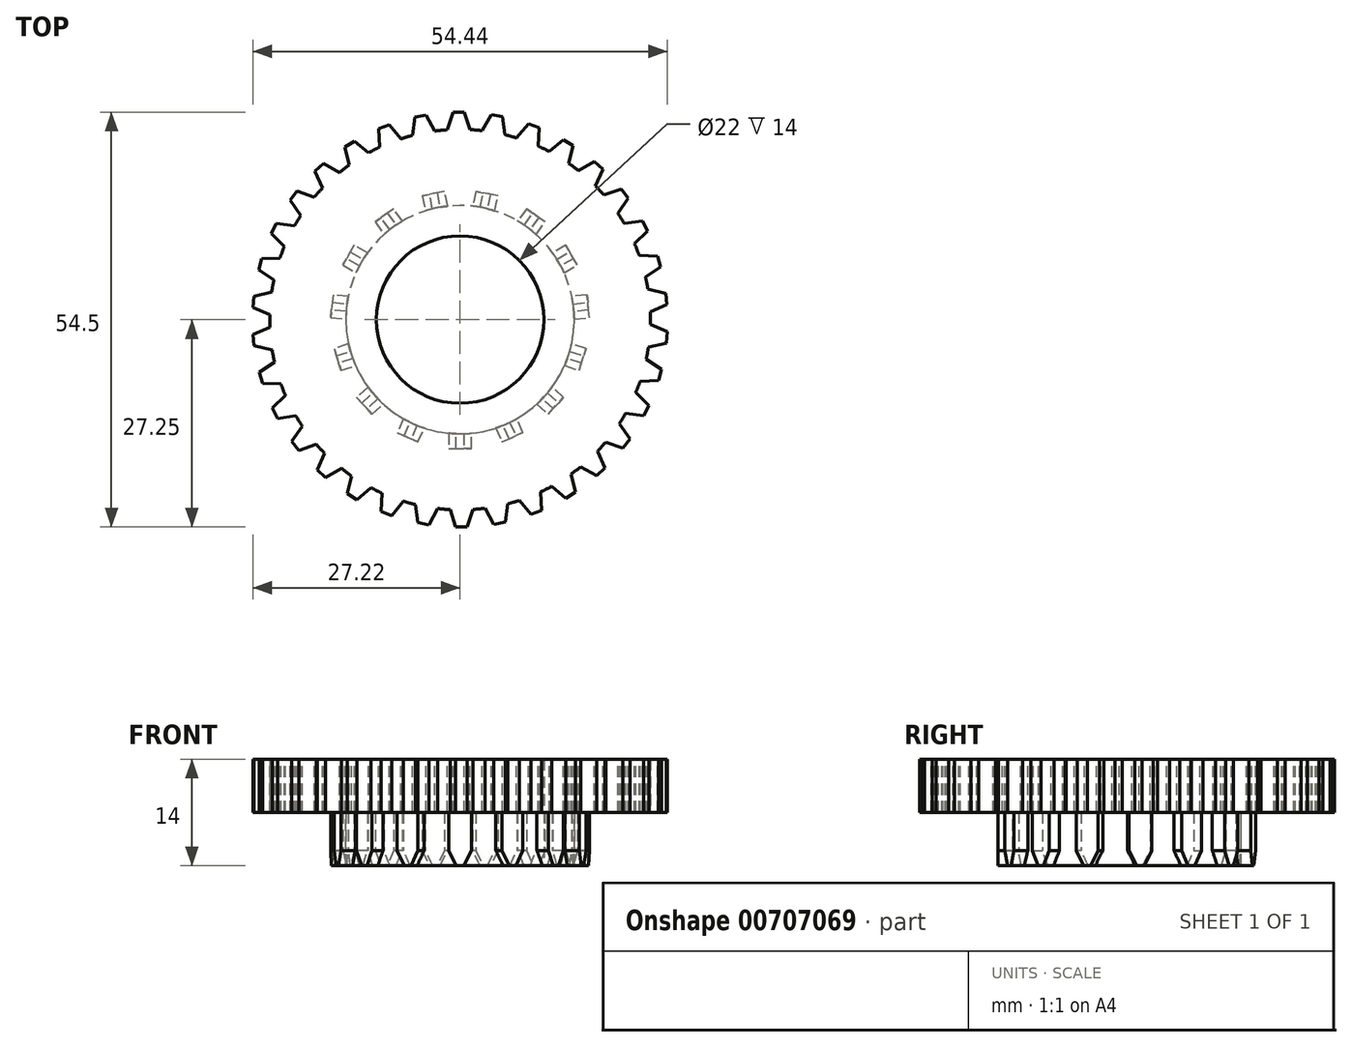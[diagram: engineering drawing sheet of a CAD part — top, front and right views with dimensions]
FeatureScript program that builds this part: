
annotation { "Feature Type Name" : "Feature", "Feature Type Description" : "" }
export const myFeature = defineFeature(function(context is Context, id is Id, definition is map)
    precondition{}
    {
        {
            var Q0;
            Q0=qCreatedBy(makeId("Top.planeOp"),FACE);
            var sketch = newSketch(context, id + "F0", { "sketchPlane" : qUnion([Q0])});
            skCircle(sketch, "E0", {"center": v(0, 0) * mm, "radius": 11 * mm});
            skCircle(sketch, "E1", {"center": v(0, 0) * mm, "radius": 25 * mm});
            skSolve(sketch);
        }
        {
            var Q0;
            Q0=makeQuery(id+"F0.imprint","IMPRINT",FACE,{"disambiguationData":[TD([[makeQuery(id+"F0.imprint","IMPRINT",EDGE,{"derivedFrom":sQuery(id+"F0.wireOp",EDGE,"E0")}),-1.0]])]});
            extrude(context, id + "F1", {"entities" : qUnion([Q0]), "depth" : 7 * mm, "offsetDistance" : 25 * mm});
        }
        {
            var Q0;
            Q0=makeQuery(id+"F1.opExtrude","CAP_FACE",FACE,{"disambiguationData":[OSD([sQuery(id+"F0.wireOp",EDGE,"E0"),sQuery(id+"F0.wireOp",EDGE,"E1")])],"isStart":false});
            var sketch = newSketch(context, id + "F2", { "sketchPlane" : qUnion([Q0])});
            skLineSegment(sketch, "E2", {"start": v(-1.69, 24.94) * mm, "end": v(1.31, 24.97) * mm});
            skLineSegment(sketch, "E3", {"start": v(1.31, 24.97) * mm, "end": v(0.56, 27.25) * mm});
            skLineSegment(sketch, "E4", {"start": v(0.56, 27.25) * mm, "end": v(-0.94, 27.25) * mm});
            skLineSegment(sketch, "E5", {"start": v(-0.94, 27.25) * mm, "end": v(-1.69, 24.94) * mm});
            skSolve(sketch);
        }
        {
            var Q0;
            {var subQ0=sQuery(id+"F2.wireOp",EDGE,"E3");Q0=makeQuery(id+"F2.imprint","IMPRINT",FACE,{"disambiguationData":[TD([[makeQuery(id+"F2.imprint","IMPRINT",EDGE,{"derivedFrom":subQ0}),1.0]])]});}
            extrude(context, id + "F3", {"entities" : qUnion([Q0]), "oppositeDirection" : true, "depth" : 7 * mm, "offsetDistance" : 25 * mm});
        }
        {
            var Q0;
            Q0=makeQuery(id+"F3.opExtrude","SWEPT_BODY",BODY,{"disambiguationData":[OSD([sQuery(id+"F0.wireOp",EDGE,"E1"),sQuery(id+"F2.wireOp",EDGE,"E3"),sQuery(id+"F2.wireOp",EDGE,"E4"),sQuery(id+"F2.wireOp",EDGE,"E5")])]});
            var Q1;
            Q1=makeQuery(id+"F1.opExtrude","CAP_EDGE",EDGE,{"disambiguationData":[OSD([sQuery(id+"F0.wireOp",EDGE,"E0")])],"isStart":false});
            circularPattern(context, id + "F4", {"entities" : qUnion([Q0]), "axis" : qUnion([Q1]), "angle" : 360 * degree, "instanceCount" : 34, "equalSpace" : true});
        }
        {
            var Q0;
            Q0=makeQuery(id+"F4.opPattern","COPY",BODY,{"derivedFrom":makeQuery(id+"F3.opExtrude","SWEPT_BODY",BODY,{"disambiguationData":[OSD([sQuery(id+"F0.wireOp",EDGE,"E1"),sQuery(id+"F2.wireOp",EDGE,"E3"),sQuery(id+"F2.wireOp",EDGE,"E4"),sQuery(id+"F2.wireOp",EDGE,"E5")])]}),"instanceName":"8"});
            var Q1;
            Q1=makeQuery(id+"F1.opExtrude","SWEPT_BODY",BODY,{"disambiguationData":[OSD([sQuery(id+"F0.wireOp",EDGE,"E0"),sQuery(id+"F0.wireOp",EDGE,"E1")])]});
            var Q2;
            Q2=makeQuery(id+"F4.opPattern","COPY",BODY,{"derivedFrom":makeQuery(id+"F3.opExtrude","SWEPT_BODY",BODY,{"disambiguationData":[OSD([sQuery(id+"F0.wireOp",EDGE,"E1"),sQuery(id+"F2.wireOp",EDGE,"E3"),sQuery(id+"F2.wireOp",EDGE,"E4"),sQuery(id+"F2.wireOp",EDGE,"E5")])]}),"instanceName":"9"});
            var Q3;
            Q3=makeQuery(id+"F4.opPattern","COPY",BODY,{"derivedFrom":makeQuery(id+"F3.opExtrude","SWEPT_BODY",BODY,{"disambiguationData":[OSD([sQuery(id+"F0.wireOp",EDGE,"E1"),sQuery(id+"F2.wireOp",EDGE,"E3"),sQuery(id+"F2.wireOp",EDGE,"E4"),sQuery(id+"F2.wireOp",EDGE,"E5")])]}),"instanceName":"10"});
            var Q4;
            Q4=makeQuery(id+"F4.opPattern","COPY",BODY,{"derivedFrom":makeQuery(id+"F3.opExtrude","SWEPT_BODY",BODY,{"disambiguationData":[OSD([sQuery(id+"F0.wireOp",EDGE,"E1"),sQuery(id+"F2.wireOp",EDGE,"E3"),sQuery(id+"F2.wireOp",EDGE,"E4"),sQuery(id+"F2.wireOp",EDGE,"E5")])]}),"instanceName":"11"});
            var Q5;
            Q5=makeQuery(id+"F4.opPattern","COPY",BODY,{"derivedFrom":makeQuery(id+"F3.opExtrude","SWEPT_BODY",BODY,{"disambiguationData":[OSD([sQuery(id+"F0.wireOp",EDGE,"E1"),sQuery(id+"F2.wireOp",EDGE,"E3"),sQuery(id+"F2.wireOp",EDGE,"E4"),sQuery(id+"F2.wireOp",EDGE,"E5")])]}),"instanceName":"12"});
            var Q6;
            Q6=makeQuery(id+"F4.opPattern","COPY",BODY,{"derivedFrom":makeQuery(id+"F3.opExtrude","SWEPT_BODY",BODY,{"disambiguationData":[OSD([sQuery(id+"F0.wireOp",EDGE,"E1"),sQuery(id+"F2.wireOp",EDGE,"E3"),sQuery(id+"F2.wireOp",EDGE,"E4"),sQuery(id+"F2.wireOp",EDGE,"E5")])]}),"instanceName":"13"});
            var Q7;
            Q7=makeQuery(id+"F4.opPattern","COPY",BODY,{"derivedFrom":makeQuery(id+"F3.opExtrude","SWEPT_BODY",BODY,{"disambiguationData":[OSD([sQuery(id+"F0.wireOp",EDGE,"E1"),sQuery(id+"F2.wireOp",EDGE,"E3"),sQuery(id+"F2.wireOp",EDGE,"E4"),sQuery(id+"F2.wireOp",EDGE,"E5")])]}),"instanceName":"33"});
            var Q8;
            Q8=makeQuery(id+"F3.opExtrude","SWEPT_BODY",BODY,{"disambiguationData":[OSD([sQuery(id+"F0.wireOp",EDGE,"E1"),sQuery(id+"F2.wireOp",EDGE,"E3"),sQuery(id+"F2.wireOp",EDGE,"E4"),sQuery(id+"F2.wireOp",EDGE,"E5")])]});
            var Q9;
            Q9=makeQuery(id+"F4.opPattern","COPY",BODY,{"derivedFrom":makeQuery(id+"F3.opExtrude","SWEPT_BODY",BODY,{"disambiguationData":[OSD([sQuery(id+"F0.wireOp",EDGE,"E1"),sQuery(id+"F2.wireOp",EDGE,"E3"),sQuery(id+"F2.wireOp",EDGE,"E4"),sQuery(id+"F2.wireOp",EDGE,"E5")])]}),"instanceName":"31"});
            var Q10;
            Q10=makeQuery(id+"F4.opPattern","COPY",BODY,{"derivedFrom":makeQuery(id+"F3.opExtrude","SWEPT_BODY",BODY,{"disambiguationData":[OSD([sQuery(id+"F0.wireOp",EDGE,"E1"),sQuery(id+"F2.wireOp",EDGE,"E3"),sQuery(id+"F2.wireOp",EDGE,"E4"),sQuery(id+"F2.wireOp",EDGE,"E5")])]}),"instanceName":"30"});
            var Q11;
            Q11=makeQuery(id+"F4.opPattern","COPY",BODY,{"derivedFrom":makeQuery(id+"F3.opExtrude","SWEPT_BODY",BODY,{"disambiguationData":[OSD([sQuery(id+"F0.wireOp",EDGE,"E1"),sQuery(id+"F2.wireOp",EDGE,"E3"),sQuery(id+"F2.wireOp",EDGE,"E4"),sQuery(id+"F2.wireOp",EDGE,"E5")])]}),"instanceName":"29"});
            var Q12;
            Q12=makeQuery(id+"F4.opPattern","COPY",BODY,{"derivedFrom":makeQuery(id+"F3.opExtrude","SWEPT_BODY",BODY,{"disambiguationData":[OSD([sQuery(id+"F0.wireOp",EDGE,"E1"),sQuery(id+"F2.wireOp",EDGE,"E3"),sQuery(id+"F2.wireOp",EDGE,"E4"),sQuery(id+"F2.wireOp",EDGE,"E5")])]}),"instanceName":"28"});
            var Q13;
            Q13=makeQuery(id+"F4.opPattern","COPY",BODY,{"derivedFrom":makeQuery(id+"F3.opExtrude","SWEPT_BODY",BODY,{"disambiguationData":[OSD([sQuery(id+"F0.wireOp",EDGE,"E1"),sQuery(id+"F2.wireOp",EDGE,"E3"),sQuery(id+"F2.wireOp",EDGE,"E4"),sQuery(id+"F2.wireOp",EDGE,"E5")])]}),"instanceName":"27"});
            var Q14;
            Q14=makeQuery(id+"F4.opPattern","COPY",BODY,{"derivedFrom":makeQuery(id+"F3.opExtrude","SWEPT_BODY",BODY,{"disambiguationData":[OSD([sQuery(id+"F0.wireOp",EDGE,"E1"),sQuery(id+"F2.wireOp",EDGE,"E3"),sQuery(id+"F2.wireOp",EDGE,"E4"),sQuery(id+"F2.wireOp",EDGE,"E5")])]}),"instanceName":"26"});
            var Q15;
            Q15=makeQuery(id+"F4.opPattern","COPY",BODY,{"derivedFrom":makeQuery(id+"F3.opExtrude","SWEPT_BODY",BODY,{"disambiguationData":[OSD([sQuery(id+"F0.wireOp",EDGE,"E1"),sQuery(id+"F2.wireOp",EDGE,"E3"),sQuery(id+"F2.wireOp",EDGE,"E4"),sQuery(id+"F2.wireOp",EDGE,"E5")])]}),"instanceName":"25"});
            var Q16;
            Q16=makeQuery(id+"F4.opPattern","COPY",BODY,{"derivedFrom":makeQuery(id+"F3.opExtrude","SWEPT_BODY",BODY,{"disambiguationData":[OSD([sQuery(id+"F0.wireOp",EDGE,"E1"),sQuery(id+"F2.wireOp",EDGE,"E3"),sQuery(id+"F2.wireOp",EDGE,"E4"),sQuery(id+"F2.wireOp",EDGE,"E5")])]}),"instanceName":"24"});
            var Q17;
            Q17=makeQuery(id+"F4.opPattern","COPY",BODY,{"derivedFrom":makeQuery(id+"F3.opExtrude","SWEPT_BODY",BODY,{"disambiguationData":[OSD([sQuery(id+"F0.wireOp",EDGE,"E1"),sQuery(id+"F2.wireOp",EDGE,"E3"),sQuery(id+"F2.wireOp",EDGE,"E4"),sQuery(id+"F2.wireOp",EDGE,"E5")])]}),"instanceName":"23"});
            var Q18;
            Q18=makeQuery(id+"F4.opPattern","COPY",BODY,{"derivedFrom":makeQuery(id+"F3.opExtrude","SWEPT_BODY",BODY,{"disambiguationData":[OSD([sQuery(id+"F0.wireOp",EDGE,"E1"),sQuery(id+"F2.wireOp",EDGE,"E3"),sQuery(id+"F2.wireOp",EDGE,"E4"),sQuery(id+"F2.wireOp",EDGE,"E5")])]}),"instanceName":"22"});
            var Q19;
            Q19=makeQuery(id+"F4.opPattern","COPY",BODY,{"derivedFrom":makeQuery(id+"F3.opExtrude","SWEPT_BODY",BODY,{"disambiguationData":[OSD([sQuery(id+"F0.wireOp",EDGE,"E1"),sQuery(id+"F2.wireOp",EDGE,"E3"),sQuery(id+"F2.wireOp",EDGE,"E4"),sQuery(id+"F2.wireOp",EDGE,"E5")])]}),"instanceName":"21"});
            var Q20;
            Q20=makeQuery(id+"F4.opPattern","COPY",BODY,{"derivedFrom":makeQuery(id+"F3.opExtrude","SWEPT_BODY",BODY,{"disambiguationData":[OSD([sQuery(id+"F0.wireOp",EDGE,"E1"),sQuery(id+"F2.wireOp",EDGE,"E3"),sQuery(id+"F2.wireOp",EDGE,"E4"),sQuery(id+"F2.wireOp",EDGE,"E5")])]}),"instanceName":"20"});
            var Q21;
            Q21=makeQuery(id+"F4.opPattern","COPY",BODY,{"derivedFrom":makeQuery(id+"F3.opExtrude","SWEPT_BODY",BODY,{"disambiguationData":[OSD([sQuery(id+"F0.wireOp",EDGE,"E1"),sQuery(id+"F2.wireOp",EDGE,"E3"),sQuery(id+"F2.wireOp",EDGE,"E4"),sQuery(id+"F2.wireOp",EDGE,"E5")])]}),"instanceName":"19"});
            var Q22;
            Q22=makeQuery(id+"F4.opPattern","COPY",BODY,{"derivedFrom":makeQuery(id+"F3.opExtrude","SWEPT_BODY",BODY,{"disambiguationData":[OSD([sQuery(id+"F0.wireOp",EDGE,"E1"),sQuery(id+"F2.wireOp",EDGE,"E3"),sQuery(id+"F2.wireOp",EDGE,"E4"),sQuery(id+"F2.wireOp",EDGE,"E5")])]}),"instanceName":"18"});
            var Q23;
            Q23=makeQuery(id+"F4.opPattern","COPY",BODY,{"derivedFrom":makeQuery(id+"F3.opExtrude","SWEPT_BODY",BODY,{"disambiguationData":[OSD([sQuery(id+"F0.wireOp",EDGE,"E1"),sQuery(id+"F2.wireOp",EDGE,"E3"),sQuery(id+"F2.wireOp",EDGE,"E4"),sQuery(id+"F2.wireOp",EDGE,"E5")])]}),"instanceName":"17"});
            var Q24;
            Q24=makeQuery(id+"F4.opPattern","COPY",BODY,{"derivedFrom":makeQuery(id+"F3.opExtrude","SWEPT_BODY",BODY,{"disambiguationData":[OSD([sQuery(id+"F0.wireOp",EDGE,"E1"),sQuery(id+"F2.wireOp",EDGE,"E3"),sQuery(id+"F2.wireOp",EDGE,"E4"),sQuery(id+"F2.wireOp",EDGE,"E5")])]}),"instanceName":"16"});
            var Q25;
            Q25=makeQuery(id+"F4.opPattern","COPY",BODY,{"derivedFrom":makeQuery(id+"F3.opExtrude","SWEPT_BODY",BODY,{"disambiguationData":[OSD([sQuery(id+"F0.wireOp",EDGE,"E1"),sQuery(id+"F2.wireOp",EDGE,"E3"),sQuery(id+"F2.wireOp",EDGE,"E4"),sQuery(id+"F2.wireOp",EDGE,"E5")])]}),"instanceName":"15"});
            var Q26;
            Q26=makeQuery(id+"F4.opPattern","COPY",BODY,{"derivedFrom":makeQuery(id+"F3.opExtrude","SWEPT_BODY",BODY,{"disambiguationData":[OSD([sQuery(id+"F0.wireOp",EDGE,"E1"),sQuery(id+"F2.wireOp",EDGE,"E3"),sQuery(id+"F2.wireOp",EDGE,"E4"),sQuery(id+"F2.wireOp",EDGE,"E5")])]}),"instanceName":"14"});
            var Q27;
            Q27=makeQuery(id+"F4.opPattern","COPY",BODY,{"derivedFrom":makeQuery(id+"F3.opExtrude","SWEPT_BODY",BODY,{"disambiguationData":[OSD([sQuery(id+"F0.wireOp",EDGE,"E1"),sQuery(id+"F2.wireOp",EDGE,"E3"),sQuery(id+"F2.wireOp",EDGE,"E4"),sQuery(id+"F2.wireOp",EDGE,"E5")])]}),"instanceName":"7"});
            var Q28;
            Q28=makeQuery(id+"F4.opPattern","COPY",BODY,{"derivedFrom":makeQuery(id+"F3.opExtrude","SWEPT_BODY",BODY,{"disambiguationData":[OSD([sQuery(id+"F0.wireOp",EDGE,"E1"),sQuery(id+"F2.wireOp",EDGE,"E3"),sQuery(id+"F2.wireOp",EDGE,"E4"),sQuery(id+"F2.wireOp",EDGE,"E5")])]}),"instanceName":"6"});
            var Q29;
            Q29=makeQuery(id+"F4.opPattern","COPY",BODY,{"derivedFrom":makeQuery(id+"F3.opExtrude","SWEPT_BODY",BODY,{"disambiguationData":[OSD([sQuery(id+"F0.wireOp",EDGE,"E1"),sQuery(id+"F2.wireOp",EDGE,"E3"),sQuery(id+"F2.wireOp",EDGE,"E4"),sQuery(id+"F2.wireOp",EDGE,"E5")])]}),"instanceName":"5"});
            var Q30;
            Q30=makeQuery(id+"F4.opPattern","COPY",BODY,{"derivedFrom":makeQuery(id+"F3.opExtrude","SWEPT_BODY",BODY,{"disambiguationData":[OSD([sQuery(id+"F0.wireOp",EDGE,"E1"),sQuery(id+"F2.wireOp",EDGE,"E3"),sQuery(id+"F2.wireOp",EDGE,"E4"),sQuery(id+"F2.wireOp",EDGE,"E5")])]}),"instanceName":"4"});
            var Q31;
            Q31=makeQuery(id+"F4.opPattern","COPY",BODY,{"derivedFrom":makeQuery(id+"F3.opExtrude","SWEPT_BODY",BODY,{"disambiguationData":[OSD([sQuery(id+"F0.wireOp",EDGE,"E1"),sQuery(id+"F2.wireOp",EDGE,"E3"),sQuery(id+"F2.wireOp",EDGE,"E4"),sQuery(id+"F2.wireOp",EDGE,"E5")])]}),"instanceName":"3"});
            var Q32;
            Q32=makeQuery(id+"F4.opPattern","COPY",BODY,{"derivedFrom":makeQuery(id+"F3.opExtrude","SWEPT_BODY",BODY,{"disambiguationData":[OSD([sQuery(id+"F0.wireOp",EDGE,"E1"),sQuery(id+"F2.wireOp",EDGE,"E3"),sQuery(id+"F2.wireOp",EDGE,"E4"),sQuery(id+"F2.wireOp",EDGE,"E5")])]}),"instanceName":"2"});
            var Q33;
            Q33=makeQuery(id+"F4.opPattern","COPY",BODY,{"derivedFrom":makeQuery(id+"F3.opExtrude","SWEPT_BODY",BODY,{"disambiguationData":[OSD([sQuery(id+"F0.wireOp",EDGE,"E1"),sQuery(id+"F2.wireOp",EDGE,"E3"),sQuery(id+"F2.wireOp",EDGE,"E4"),sQuery(id+"F2.wireOp",EDGE,"E5")])]}),"instanceName":"1"});
            var Q34;
            Q34=makeQuery(id+"F4.opPattern","COPY",BODY,{"derivedFrom":makeQuery(id+"F3.opExtrude","SWEPT_BODY",BODY,{"disambiguationData":[OSD([sQuery(id+"F0.wireOp",EDGE,"E1"),sQuery(id+"F2.wireOp",EDGE,"E3"),sQuery(id+"F2.wireOp",EDGE,"E4"),sQuery(id+"F2.wireOp",EDGE,"E5")])]}),"instanceName":"32"});
            booleanBodies(context, id + "F5", {"operationType" : BooleanOperationType.UNION, "tools" : qUnion([Q0, Q1, Q2, Q3, Q4, Q5, Q6, Q7, Q8, Q9, Q10, Q11, Q12, Q13, Q14, Q15, Q16, Q17, Q18, Q19, Q20, Q21, Q22, Q23, Q24, Q25, Q26, Q27, Q28, Q29, Q30, Q31, Q32, Q33, Q34])});
        }
        {
            var Q0;
            {var subQ0=sQuery(id+"F0.wireOp",EDGE,"E1");var subQ1=makeQuery(id+"F3.opExtrude","CAP_FACE",FACE,{"disambiguationData":[OSD([subQ0,sQuery(id+"F2.wireOp",EDGE,"E3"),sQuery(id+"F2.wireOp",EDGE,"E4"),sQuery(id+"F2.wireOp",EDGE,"E5")])],"isStart":false});Q0=makeQuery(id+"F5.opBoolean","MERGE",FACE,{"derivedFrom":[makeQuery(id+"F1.opExtrude","CAP_FACE",FACE,{"disambiguationData":[OSD([sQuery(id+"F0.wireOp",EDGE,"E0"),subQ0])],"isStart":true}),subQ1,makeQuery(id+"F4.opPattern","COPY",FACE,{"derivedFrom":subQ1,"instanceName":"1"}),makeQuery(id+"F4.opPattern","COPY",FACE,{"derivedFrom":subQ1,"instanceName":"2"}),makeQuery(id+"F4.opPattern","COPY",FACE,{"derivedFrom":subQ1,"instanceName":"3"}),makeQuery(id+"F4.opPattern","COPY",FACE,{"derivedFrom":subQ1,"instanceName":"4"}),makeQuery(id+"F4.opPattern","COPY",FACE,{"derivedFrom":subQ1,"instanceName":"5"}),makeQuery(id+"F4.opPattern","COPY",FACE,{"derivedFrom":subQ1,"instanceName":"6"}),makeQuery(id+"F4.opPattern","COPY",FACE,{"derivedFrom":subQ1,"instanceName":"7"}),makeQuery(id+"F4.opPattern","COPY",FACE,{"derivedFrom":subQ1,"instanceName":"8"}),makeQuery(id+"F4.opPattern","COPY",FACE,{"derivedFrom":subQ1,"instanceName":"9"}),makeQuery(id+"F4.opPattern","COPY",FACE,{"derivedFrom":subQ1,"instanceName":"10"}),makeQuery(id+"F4.opPattern","COPY",FACE,{"derivedFrom":subQ1,"instanceName":"11"}),makeQuery(id+"F4.opPattern","COPY",FACE,{"derivedFrom":subQ1,"instanceName":"12"}),makeQuery(id+"F4.opPattern","COPY",FACE,{"derivedFrom":subQ1,"instanceName":"13"}),makeQuery(id+"F4.opPattern","COPY",FACE,{"derivedFrom":subQ1,"instanceName":"14"}),makeQuery(id+"F4.opPattern","COPY",FACE,{"derivedFrom":subQ1,"instanceName":"15"}),makeQuery(id+"F4.opPattern","COPY",FACE,{"derivedFrom":subQ1,"instanceName":"16"}),makeQuery(id+"F4.opPattern","COPY",FACE,{"derivedFrom":subQ1,"instanceName":"17"}),makeQuery(id+"F4.opPattern","COPY",FACE,{"derivedFrom":subQ1,"instanceName":"18"}),makeQuery(id+"F4.opPattern","COPY",FACE,{"derivedFrom":subQ1,"instanceName":"19"}),makeQuery(id+"F4.opPattern","COPY",FACE,{"derivedFrom":subQ1,"instanceName":"20"}),makeQuery(id+"F4.opPattern","COPY",FACE,{"derivedFrom":subQ1,"instanceName":"21"}),makeQuery(id+"F4.opPattern","COPY",FACE,{"derivedFrom":subQ1,"instanceName":"22"}),makeQuery(id+"F4.opPattern","COPY",FACE,{"derivedFrom":subQ1,"instanceName":"23"}),makeQuery(id+"F4.opPattern","COPY",FACE,{"derivedFrom":subQ1,"instanceName":"24"}),makeQuery(id+"F4.opPattern","COPY",FACE,{"derivedFrom":subQ1,"instanceName":"25"}),makeQuery(id+"F4.opPattern","COPY",FACE,{"derivedFrom":subQ1,"instanceName":"26"}),makeQuery(id+"F4.opPattern","COPY",FACE,{"derivedFrom":subQ1,"instanceName":"27"}),makeQuery(id+"F4.opPattern","COPY",FACE,{"derivedFrom":subQ1,"instanceName":"28"}),makeQuery(id+"F4.opPattern","COPY",FACE,{"derivedFrom":subQ1,"instanceName":"29"}),makeQuery(id+"F4.opPattern","COPY",FACE,{"derivedFrom":subQ1,"instanceName":"30"}),makeQuery(id+"F4.opPattern","COPY",FACE,{"derivedFrom":subQ1,"instanceName":"31"}),makeQuery(id+"F4.opPattern","COPY",FACE,{"derivedFrom":subQ1,"instanceName":"32"}),makeQuery(id+"F4.opPattern","COPY",FACE,{"derivedFrom":subQ1,"instanceName":"33"})]});}
            var sketch = newSketch(context, id + "F6", { "sketchPlane" : qUnion([Q0])});
            skCircle(sketch, "E6", {"center": v(0, 0) * mm, "radius": 15 * mm});
            skSolve(sketch);
        }
        {
            var Q0;
            Q0=makeQuery(id+"F6.imprint","IMPRINT",FACE,{"disambiguationData":[TD([[makeQuery(id+"F6.imprint","IMPRINT",EDGE,{"derivedFrom":sQuery(id+"F6.wireOp",EDGE,"E6")}),1.0]])]});
            extrude(context, id + "F7", {"entities" : qUnion([Q0]), "operationType" : NewBodyOperationType.ADD, "depth" : 7 * mm, "offsetDistance" : 25 * mm});
        }
        {
            var Q0;
            Q0=makeQuery(id+"F7.opExtrude","CAP_FACE",FACE,{"disambiguationData":[OSD([sQuery(id+"F0.wireOp",EDGE,"E0"),sQuery(id+"F6.wireOp",EDGE,"E6")])],"isStart":false});
            var sketch = newSketch(context, id + "F8", { "sketchPlane" : qUnion([Q0])});
            skLineSegment(sketch, "E7", {"start": v(-1.5, 14.92) * mm, "end": v(1.5, 14.92) * mm});
            skLineSegment(sketch, "E8.top", {"start": v(-1.5, 16.92) * mm, "end": v(1.5, 16.92) * mm});
            skLineSegment(sketch, "E8.left", {"start": v(-1.5, 14.92) * mm, "end": v(-1.5, 16.92) * mm});
            skLineSegment(sketch, "E8.right", {"start": v(1.5, 14.92) * mm, "end": v(1.5, 16.92) * mm});
            skSolve(sketch);
        }
        {
            var Q0;
            Q0=makeQuery(id+"F8.imprint","IMPRINT",FACE,{"disambiguationData":[TD([[makeQuery(id+"F8.imprint","IMPRINT",EDGE,{"derivedFrom":sQuery(id+"F8.wireOp",EDGE,"E8.top")}),-1.0]])]});
            extrude(context, id + "F9", {"entities" : qUnion([Q0]), "oppositeDirection" : true, "depth" : 7 * mm, "offsetDistance" : 25 * mm});
        }
        {
            var Q0;
            Q0=makeQuery(id+"F9.opExtrude","CAP_EDGE",EDGE,{"disambiguationData":[OSD([sQuery(id+"F8.wireOp",EDGE,"E8.left")])],"isStart":true});
            var Q1;
            Q1=makeQuery(id+"F9.opExtrude","CAP_EDGE",EDGE,{"disambiguationData":[OSD([sQuery(id+"F8.wireOp",EDGE,"E8.right")])],"isStart":true});
            chamfer(context, id + "F10", {"entities" : qUnion([Q0, Q1]), "chamferType" : ChamferType.TWO_OFFSETS, "width1" : 2 * mm, "oppositeDirection" : false, "width2" : 1 * mm, "tangentPropagation" : true});
        }
        {
            var Q0;
            Q0=makeQuery(id+"F9.opExtrude","SWEPT_BODY",BODY,{"disambiguationData":[OSD([sQuery(id+"F6.wireOp",EDGE,"E6"),sQuery(id+"F8.wireOp",EDGE,"E8.top"),sQuery(id+"F8.wireOp",EDGE,"E8.left"),sQuery(id+"F8.wireOp",EDGE,"E8.right")])]});
            var Q1;
            Q1=makeQuery(id+"F7.opExtrude","CAP_EDGE",EDGE,{"disambiguationData":[OSD([sQuery(id+"F0.wireOp",EDGE,"E0")])],"isStart":false});
            circularPattern(context, id + "F11", {"entities" : qUnion([Q0]), "axis" : qUnion([Q1]), "angle" : 360 * degree, "instanceCount" : 15, "equalSpace" : true});
        }
    });
